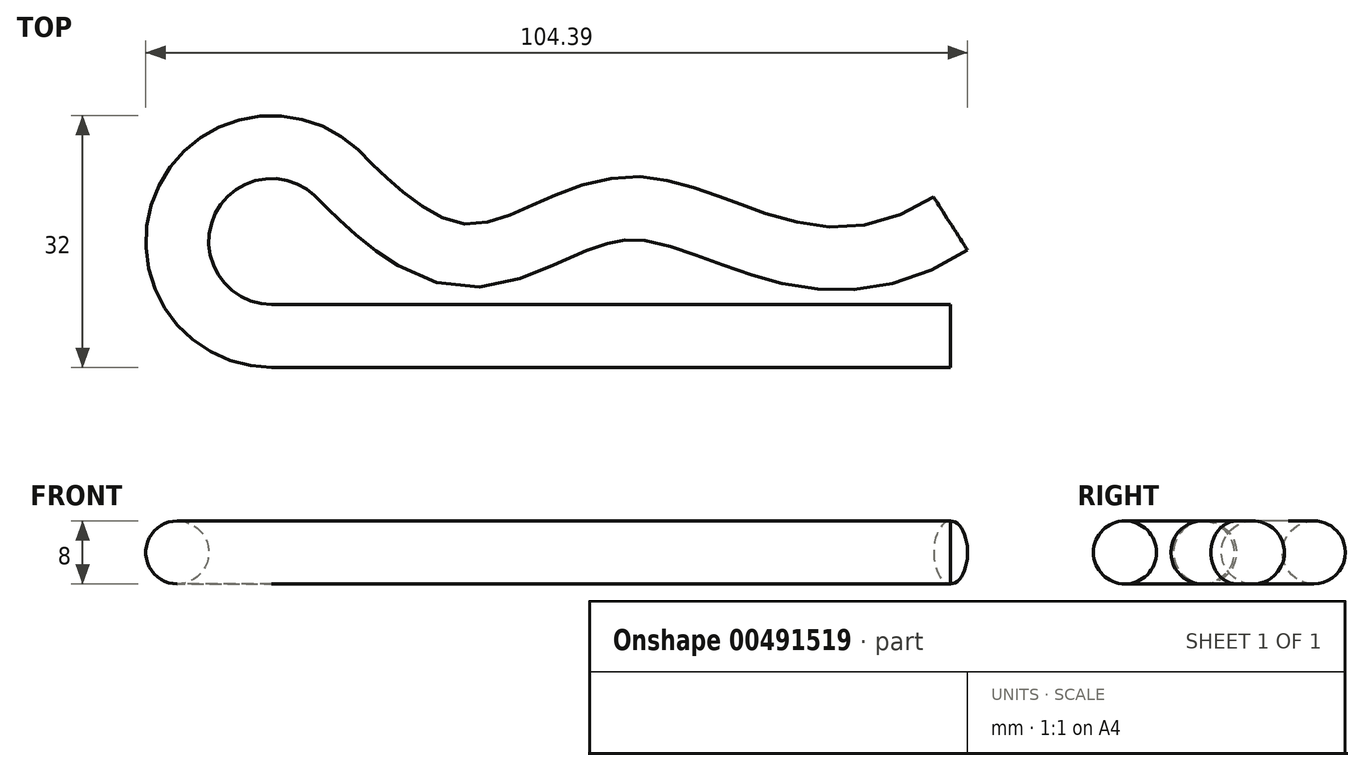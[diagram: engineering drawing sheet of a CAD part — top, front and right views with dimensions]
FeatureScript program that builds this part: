
annotation { "Feature Type Name" : "Feature", "Feature Type Description" : "" }
export const myFeature = defineFeature(function(context is Context, id is Id, definition is map)
    precondition{}
    {
        {
            var Q0;
            Q0=qCreatedBy(makeId("Top.planeOp"),FACE);
            var sketch = newSketch(context, id + "F0", { "sketchPlane" : qUnion([Q0])});
            skCircle(sketch, "E0", {"center": v(0, 0) * mm, "radius": 10 * mm, "construction": true});
            skLineSegment(sketch, "E1", {"start": v(40.17, 0) * mm, "end": v(-46.07, 0) * mm});
            skArc(sketch, "E2", {"start": v(-46.07, 0) * mm, "mid": v(-57.23, 16.41) * mm, "end": v(-37.86, 20.75) * mm});
            skFitSpline(sketch, "E3", {"points": [v(-37.86, 20.75) * mm, v(-22.66, 10.31) * mm, v(0, 16.25) * mm, v(40.17, 14.26) * mm], "startDerivative": vector(16.86, -15.81) * mm, "endDerivative": vector(125.72, 80.32) * mm});
            skSolve(sketch);
        }
        {
            var Q0;
            Q0=qCreatedBy(makeId("Right.planeOp"),FACE);
            var Q1;
            Q1=sQuery(id+"F0.wireOp",VERTEX,"E1.start");
            cPlane(context, id + "F1", {"entities" : qUnion([Q0, Q1]), "cplaneType" : CPlaneType.PLANE_POINT, "offset" : 25 * mm, "width" : 150 * mm, "height" : 150 * mm});
        }
        {
            var Q0;
            Q0=qCreatedBy(id+"F1.planeOp",FACE);
            var sketch = newSketch(context, id + "F2", { "sketchPlane" : qUnion([Q0])});
            skCircle(sketch, "E4", {"center": v(0, 0) * mm, "radius": 4 * mm});
            skSolve(sketch);
        }
        {
            var Q0;
            Q0=makeQuery(id+"F2.imprint","IMPRINT",FACE,{"disambiguationData":[TD([[makeQuery(id+"F2.imprint","IMPRINT",EDGE,{"derivedFrom":sQuery(id+"F2.wireOp",EDGE,"E4")}),1.0]])]});
            var Q1;
            Q1=sQuery(id+"F2.wireOp",EDGE,"E4");
            var Q2;
            Q2=qConstructionFilter(qBodyType(qCreatedBy(id+"F0",EDGE),BodyType.WIRE),ConstructionObject.NO);
            sweep(context, id + "F3", {"profiles" : qUnion([Q0]), "surfaceProfiles" : qUnion([Q1]), "path" : qUnion([Q2])});
        }
    });
